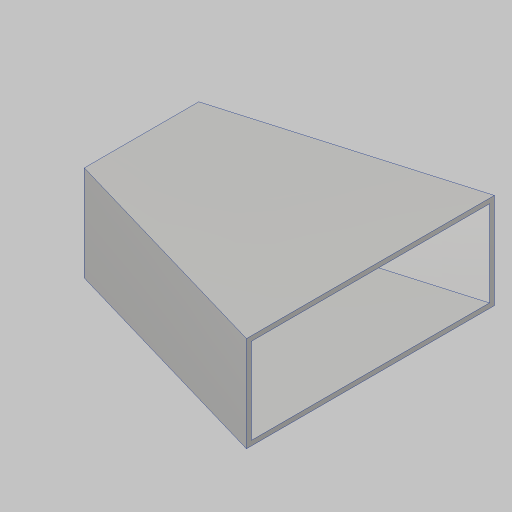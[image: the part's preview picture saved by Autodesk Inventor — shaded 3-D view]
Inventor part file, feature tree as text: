
AUTODESK INVENTOR PART (.ipt)
format: ipt  version: 2023.5 (Build 275446000, 446)  size: 92,672 bytes
history: native  units: in
note: dims shown in document units (in); Inventor stores cm internally (conversion verified against a paired STEP export)
features: extrude x1, shell x1, sketch x1
ambient origin geometry x8: Origin, YZ Plane, XZ Plane, XY Plane, X Axis, Y Axis, Z Axis, Center Point
bodies: Solid1 (feature_tree)
feature tree (3):
  extrude  "Extrusion1"  Depth=6.0in
  shell  "Shell1"  Thickness=12.0in
  sketch  "Sketch1"  dims[d0=13.0in d1=6.0in d2=12.0in d3=5.0in d4=0.0in d5=0.25in]
